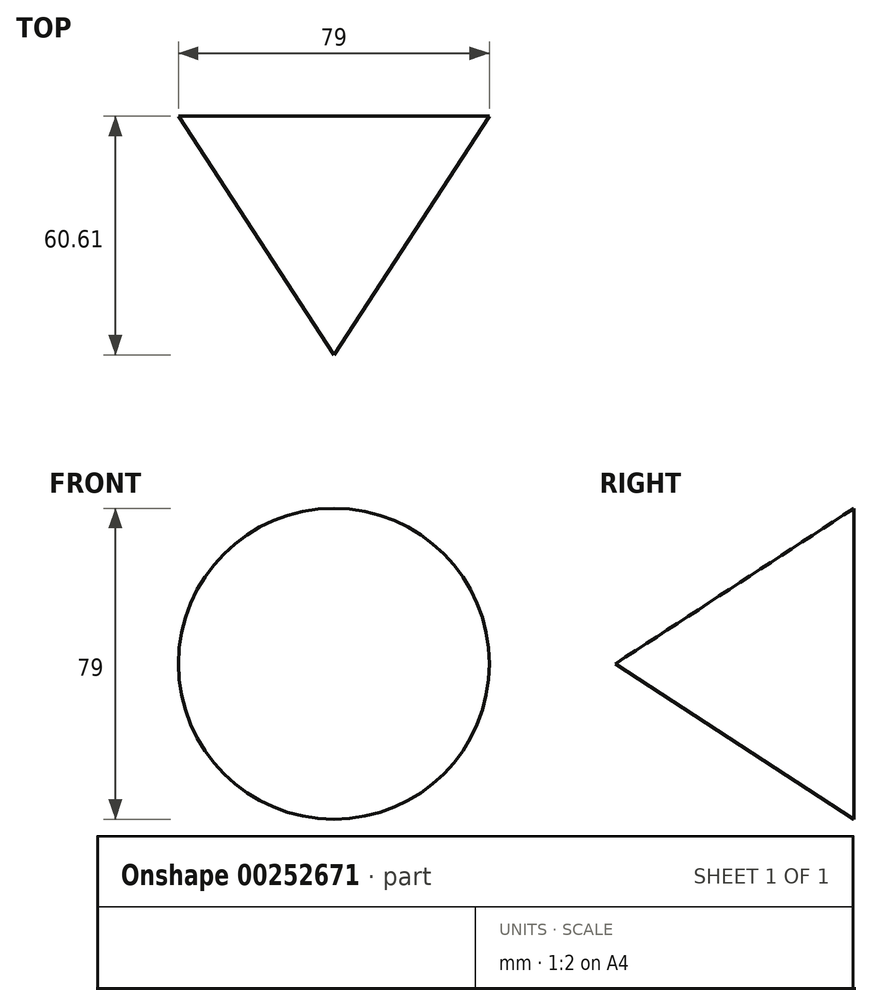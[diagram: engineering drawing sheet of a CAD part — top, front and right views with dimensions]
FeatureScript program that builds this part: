
annotation { "Feature Type Name" : "Feature", "Feature Type Description" : "" }
export const myFeature = defineFeature(function(context is Context, id is Id, definition is map)
    precondition{}
    {
        {
            var Q0;
            Q0=qCreatedBy(makeId("Front.planeOp"),FACE);
            var sketch = newSketch(context, id + "F0", { "sketchPlane" : qUnion([Q0])});
            skCircle(sketch, "E0", {"center": v(0, 0) * mm, "radius": 39.5 * mm});
            skSolve(sketch);
        }
        {
            var Q0;
            Q0=qCreatedBy(makeId("Top.planeOp"),FACE);
            var sketch = newSketch(context, id + "F1", { "sketchPlane" : qUnion([Q0])});
            skLineSegment(sketch, "E1", {"start": v(0, 0) * mm, "end": v(0, -60.61) * mm});
            skSolve(sketch);
        }
        {
            var Q0;
            Q0=makeQuery(id+"F0.imprint","IMPRINT",FACE,{"disambiguationData":[TD([[makeQuery(id+"F0.imprint","IMPRINT",EDGE,{"derivedFrom":sQuery(id+"F0.wireOp",EDGE,"E0")}),1.0]])]});
            var Q1;
            Q1=sQuery(id+"F1.wireOp",VERTEX,"E1.end");
            loft(context, id + "F2", {"sheetProfilesArray" : [{ "sheetProfileEntities" : qUnion([Q0]) }, { "sheetProfileEntities" : qUnion([Q1]) }]});
        }
    });
